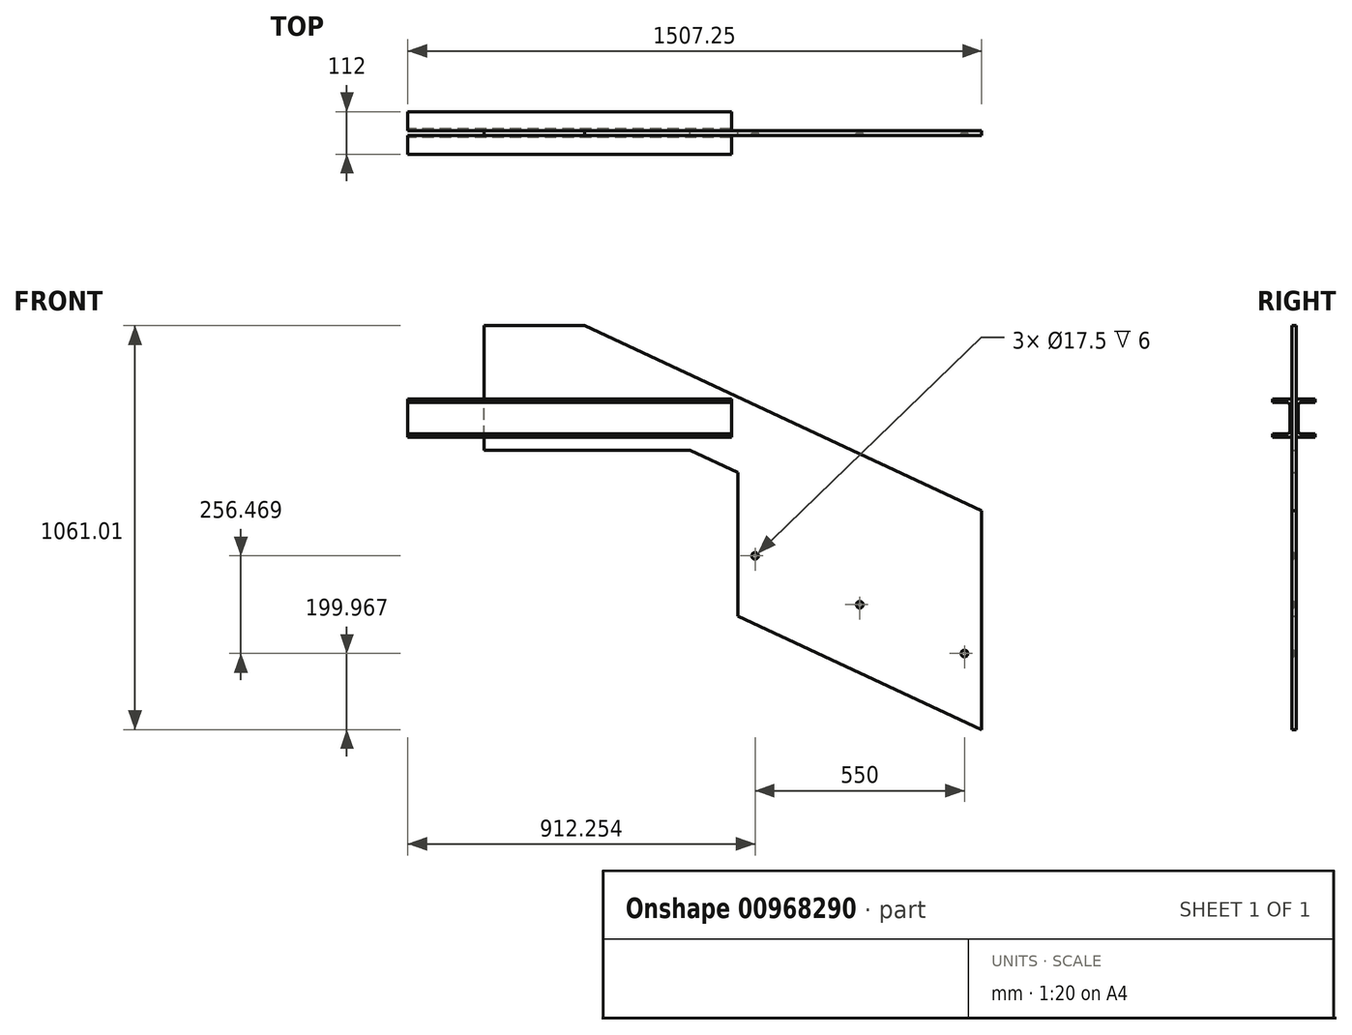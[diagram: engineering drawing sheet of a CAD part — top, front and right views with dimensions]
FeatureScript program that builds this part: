
annotation { "Feature Type Name" : "Feature", "Feature Type Description" : "" }
export const myFeature = defineFeature(function(context is Context, id is Id, definition is map)
    precondition{}
    {
        {
            var Q0;
            Q0=qCreatedBy(makeId("Front.planeOp"),FACE);
            var sketch = newSketch(context, id + "F0", { "sketchPlane" : qUnion([Q0])});
            skLineSegment(sketch, "E0", {"start": v(0, 0) * mm, "end": v(265, 0) * mm});
            skLineSegment(sketch, "E1", {"start": v(265, 0) * mm, "end": v(1307.25, -486.01) * mm});
            skLineSegment(sketch, "E2", {"start": v(1307.25, -486.01) * mm, "end": v(1307.25, -1061.01) * mm});
            skLineSegment(sketch, "E3", {"start": v(1307.25, -1061.01) * mm, "end": v(667.25, -762.57) * mm});
            skLineSegment(sketch, "E4", {"start": v(667.25, -762.57) * mm, "end": v(667.25, -385.87) * mm});
            skLineSegment(sketch, "E5", {"start": v(667.25, -385.87) * mm, "end": v(541, -327) * mm});
            skLineSegment(sketch, "E6", {"start": v(541, -327) * mm, "end": v(0, -327) * mm});
            skLineSegment(sketch, "E7", {"start": v(0, -327) * mm, "end": v(0, 0) * mm});
            skPoint(sketch, "E8", {"position": v(712.25, -604.57) * mm});
            skPoint(sketch, "E9", {"position": v(987.25, -732.8) * mm});
            skPoint(sketch, "E10", {"position": v(1262.25, -861.04) * mm});
            skLineSegment(sketch, "E11", {"start": v(712.25, -604.57) * mm, "end": v(1262.25, -861.04) * mm, "construction": true});
            skSolve(sketch);
        }
        {
            var Q0;
            Q0=makeQuery(id+"F0.imprint","IMPRINT",FACE,{"disambiguationData":[TD([[makeQuery(id+"F0.imprint","IMPRINT",EDGE,{"derivedFrom":sQuery(id+"F0.wireOp",EDGE,"E0")}),-1.0]])]});
            extrude(context, id + "F1", {"entities" : qUnion([Q0]), "endBound" : BoundingType.SYMMETRIC, "depth" : 12 * mm, "offsetDistance" : 25 * mm});
        }
        {
            var Q0;
            Q0=sQuery(id+"F0.wireOp",VERTEX,"E8");
            var Q1;
            Q1=sQuery(id+"F0.wireOp",VERTEX,"E9");
            var Q2;
            Q2=sQuery(id+"F0.wireOp",VERTEX,"E10");
            var Q3;
            Q3=makeQuery(id+"F1.opExtrude","SWEPT_BODY",BODY,{"disambiguationData":[OSD([sQuery(id+"F0.wireOp",EDGE,"E0"),sQuery(id+"F0.wireOp",EDGE,"E1"),sQuery(id+"F0.wireOp",EDGE,"E2"),sQuery(id+"F0.wireOp",EDGE,"E3"),sQuery(id+"F0.wireOp",EDGE,"E4"),sQuery(id+"F0.wireOp",EDGE,"E5"),sQuery(id+"F0.wireOp",EDGE,"E6"),sQuery(id+"F0.wireOp",EDGE,"E7")])]});
            hole(context, id + "F2", {"style" : HoleStyle.SIMPLE, "endStyle" : HoleEndStyle.THROUGH, "oppositeDirection" : true, "standardTappedOrClearance" : lookupTablePath({ "fit" : "Normal", "standard" : "ISO", "size" : "M16", "type" : "Clearance" }), "standardBlindInLast" : lookupTablePath({ "fit" : "Normal", "standard" : "ISO", "engagement" : "75%", "pitch" : "2 mm", "size" : "M16", "type" : "Clearance & tapped" }), "holeDiameter" : 17.5 * mm, "majorDiameter" : 5 * mm, "isTappedThrough" : true, "tappedDepth" : 12 * mm, "tapClearance" : 3, "locations" : qUnion([Q0, Q1, Q2]), "scope" : qUnion([Q3])});
        }
        {
            var Q0;
            Q0=qCreatedBy(makeId("Right.planeOp"),FACE);
            var sketch = newSketch(context, id + "F3", { "sketchPlane" : qUnion([Q0])});
            skLineSegment(sketch, "E12", {"start": v(-56, -193) * mm, "end": v(-6, -193) * mm});
            skLineSegment(sketch, "E13", {"start": v(-6, -193) * mm, "end": v(-6, -293) * mm});
            skLineSegment(sketch, "E14", {"start": v(-6, -293) * mm, "end": v(-56, -293) * mm});
            skLineSegment(sketch, "E15", {"start": v(-56, -293) * mm, "end": v(-56, -284.6) * mm});
            skLineSegment(sketch, "E16", {"start": v(-56, -284.6) * mm, "end": v(-19.4, -284.6) * mm});
            skLineSegment(sketch, "E17", {"start": v(-11, -276.2) * mm, "end": v(-11, -209.8) * mm});
            skLineSegment(sketch, "E18", {"start": v(-19.4, -201.4) * mm, "end": v(-56, -201.4) * mm});
            skLineSegment(sketch, "E19", {"start": v(-56, -201.4) * mm, "end": v(-56, -193) * mm});
            skPoint(sketch, "E20.visualSharp", {"position": v(-11, -201.4) * mm});
            skArc(sketch, "E20.filletArc", {"start": v(-11, -209.8) * mm, "mid": v(-13.46, -203.86) * mm, "end": v(-19.4, -201.4) * mm});
            skPoint(sketch, "E21.visualSharp", {"position": v(-11, -284.6) * mm});
            skArc(sketch, "E21.filletArc", {"start": v(-19.4, -284.6) * mm, "mid": v(-13.46, -282.14) * mm, "end": v(-11, -276.2) * mm});
            skSolve(sketch);
        }
        {
            var Q0;
            Q0=makeQuery(id+"F3.imprint","IMPRINT",FACE,{"disambiguationData":[TD([[makeQuery(id+"F3.imprint","IMPRINT",EDGE,{"derivedFrom":sQuery(id+"F3.wireOp",EDGE,"E12")}),-1.0]])]});
            var Q1;
            Q1=makeQuery(id+"F1.opExtrude","SWEPT_FACE",FACE,{"disambiguationData":[OSD([sQuery(id+"F0.wireOp",EDGE,"E1")])]});
            extrude(context, id + "F4", {"entities" : qUnion([Q0]), "depth" : 650 * mm, "endBoundEntityFace" : qUnion([Q1]), "offsetDistance" : 25 * mm, "hasSecondDirection" : true, "secondDirectionOppositeDirection" : true, "secondDirectionDepth" : 200 * mm});
        }
        {
            var Q0;
            Q0=makeQuery(id+"F4.opExtrude","SWEPT_BODY",BODY,{"disambiguationData":[OSD([sQuery(id+"F3.wireOp",EDGE,"E12"),sQuery(id+"F3.wireOp",EDGE,"E13"),sQuery(id+"F3.wireOp",EDGE,"E14"),sQuery(id+"F3.wireOp",EDGE,"E15"),sQuery(id+"F3.wireOp",EDGE,"E16"),sQuery(id+"F3.wireOp",EDGE,"E17"),sQuery(id+"F3.wireOp",EDGE,"E18"),sQuery(id+"F3.wireOp",EDGE,"E19"),sQuery(id+"F3.wireOp",EDGE,"E20.filletArc"),sQuery(id+"F3.wireOp",EDGE,"E21.filletArc")])]});
            var Q1;
            Q1=qCreatedBy(makeId("Front.planeOp"),FACE);
            mirror(context, id + "F5", {"entities" : qUnion([Q0]), "mirrorPlane" : qUnion([Q1])});
        }
    });
